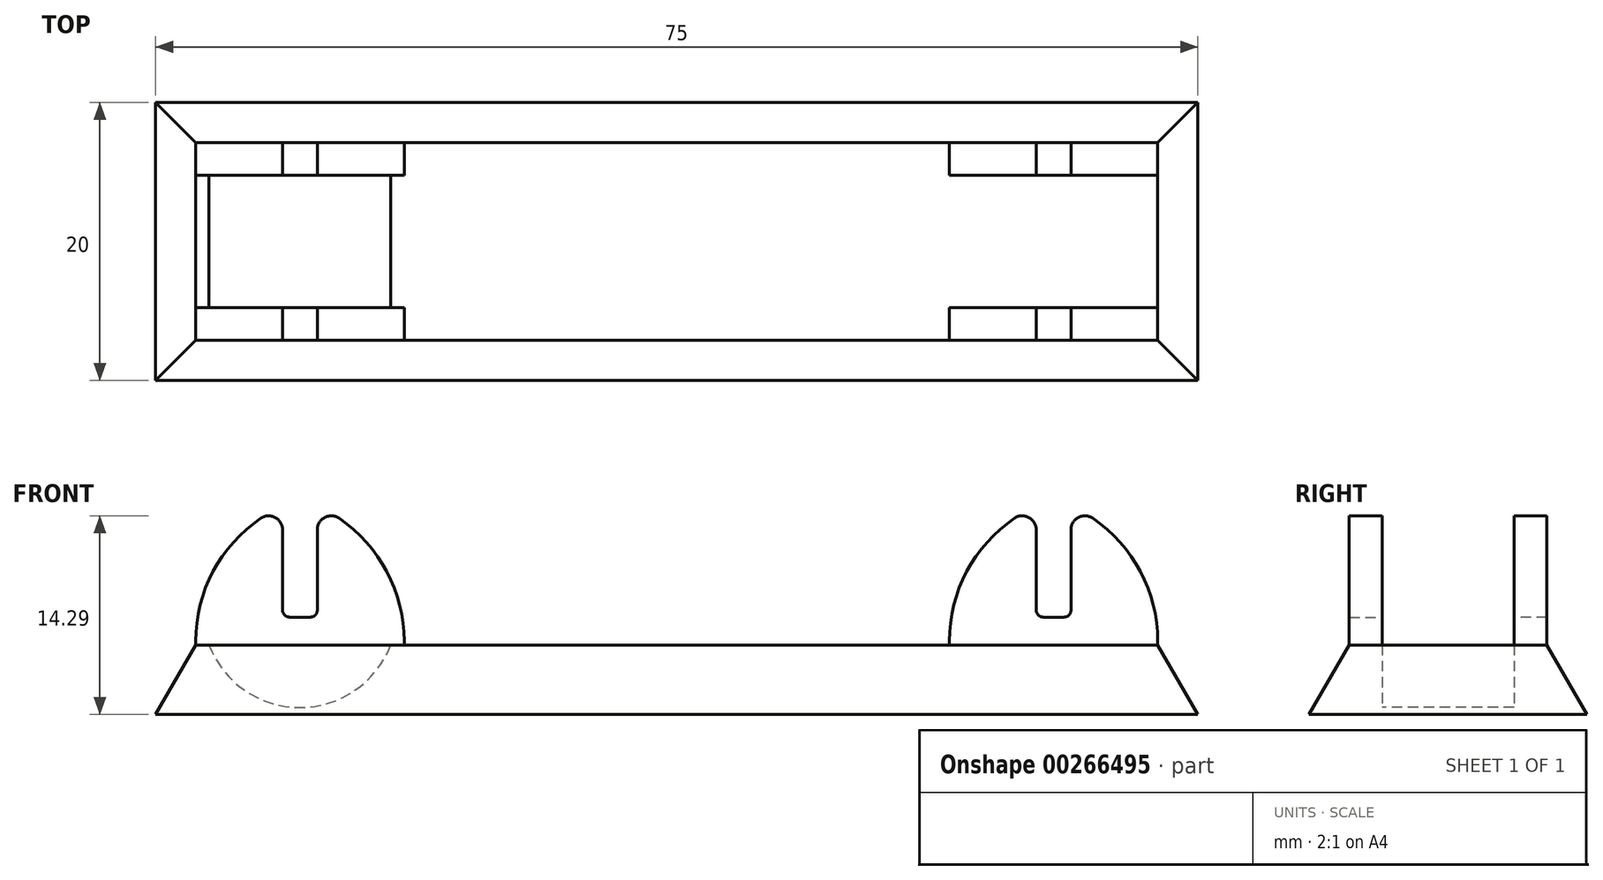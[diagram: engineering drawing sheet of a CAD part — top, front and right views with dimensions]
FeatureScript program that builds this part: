
annotation { "Feature Type Name" : "Feature", "Feature Type Description" : "" }
export const myFeature = defineFeature(function(context is Context, id is Id, definition is map)
    precondition{}
    {
        {
            var Q0;
            Q0=qCreatedBy(makeId("Top.planeOp"),FACE);
            var sketch = newSketch(context, id + "F0", { "sketchPlane" : qUnion([Q0])});
            skLineSegment(sketch, "E0.bottom", {"start": v(-37.5, 10) * mm, "end": v(37.5, 10) * mm});
            skLineSegment(sketch, "E0.top", {"start": v(-37.5, -10) * mm, "end": v(37.5, -10) * mm});
            skLineSegment(sketch, "E0.left", {"start": v(-37.5, 10) * mm, "end": v(-37.5, -10) * mm});
            skLineSegment(sketch, "E0.right", {"start": v(37.5, 10) * mm, "end": v(37.5, -10) * mm});
            skPoint(sketch, "E1", {"position": v(0, 10) * mm});
            skPoint(sketch, "E2", {"position": v(-37.5, 0) * mm});
            skSolve(sketch);
        }
        {
            var Q0;
            Q0=makeQuery(id+"F0.imprint","IMPRINT",FACE,{"disambiguationData":[TD([[makeQuery(id+"F0.imprint","IMPRINT",EDGE,{"derivedFrom":sQuery(id+"F0.wireOp",EDGE,"E0.bottom")}),-1.0]])]});
            extrude(context, id + "F1", {"entities" : qUnion([Q0]), "depth" : 5 * mm, "hasDraft" : true, "draftAngle" : 30 * degree, "draftPullDirection" : true});
        }
        {
            var Q0;
            Q0=makeQuery(id+"F1.opExtrude","CAP_FACE",FACE,{"disambiguationData":[OSD([sQuery(id+"F0.wireOp",EDGE,"E0.bottom"),sQuery(id+"F0.wireOp",EDGE,"E0.top"),sQuery(id+"F0.wireOp",EDGE,"E0.left"),sQuery(id+"F0.wireOp",EDGE,"E0.right")])],"isStart":false});
            var sketch = newSketch(context, id + "F2", { "sketchPlane" : qUnion([Q0])});
            skLineSegment(sketch, "E3.bottom", {"start": v(-34.61, 7.11) * mm, "end": v(-19.61, 7.11) * mm});
            skLineSegment(sketch, "E3.top", {"start": v(-34.61, 4.75) * mm, "end": v(-19.61, 4.75) * mm});
            skLineSegment(sketch, "E3.left", {"start": v(-34.61, 7.11) * mm, "end": v(-34.61, 4.75) * mm});
            skLineSegment(sketch, "E3.right", {"start": v(-19.61, 7.11) * mm, "end": v(-19.61, 4.75) * mm});
            skLineSegment(sketch, "E4", {"start": v(-57.2, 0) * mm, "end": v(85.15, 0) * mm, "construction": true});
            skLineSegment(sketch, "E5.MirrorCS", {"start": v(-19.61, -7.11) * mm, "end": v(-19.61, -4.75) * mm});
            skLineSegment(sketch, "E6.MirrorCS", {"start": v(-34.61, -7.11) * mm, "end": v(-19.61, -7.11) * mm});
            skLineSegment(sketch, "E7.MirrorCS", {"start": v(-34.61, -4.75) * mm, "end": v(-19.61, -4.75) * mm});
            skLineSegment(sketch, "E8.MirrorCS", {"start": v(-34.61, -7.11) * mm, "end": v(-34.61, -4.75) * mm});
            skSolve(sketch);
        }
        {
            var Q0;
            Q0=makeQuery(id+"F2.imprint","IMPRINT",FACE,{"disambiguationData":[TD([[makeQuery(id+"F2.imprint","IMPRINT",EDGE,{"derivedFrom":sQuery(id+"F2.wireOp",EDGE,"E3.bottom")}),-1.0]])]});
            var Q1;
            Q1=makeQuery(id+"F2.imprint","IMPRINT",FACE,{"disambiguationData":[TD([[makeQuery(id+"F2.imprint","IMPRINT",EDGE,{"derivedFrom":sQuery(id+"F2.wireOp",EDGE,"E5.MirrorCS")}),1.0]])]});
            extrude(context, id + "F3", {"entities" : qUnion([Q0, Q1]), "depth" : 10 * mm});
        }
        {
            var Q0;
            Q0=makeQuery(id+"F3.opExtrude","CAP_FACE",FACE,{"disambiguationData":[OSD([sQuery(id+"F2.wireOp",EDGE,"E3.bottom"),sQuery(id+"F2.wireOp",EDGE,"E3.top"),sQuery(id+"F2.wireOp",EDGE,"E3.left"),sQuery(id+"F2.wireOp",EDGE,"E3.right")])],"isStart":false});
            var sketch = newSketch(context, id + "F4", { "sketchPlane" : qUnion([Q0])});
            skLineSegment(sketch, "E9.bottom", {"start": v(-28.36, 7.11) * mm, "end": v(-25.86, 7.11) * mm});
            skLineSegment(sketch, "E9.top", {"start": v(-28.36, 4.75) * mm, "end": v(-25.86, 4.75) * mm});
            skLineSegment(sketch, "E9.left", {"start": v(-28.36, 7.11) * mm, "end": v(-28.36, 4.75) * mm});
            skLineSegment(sketch, "E9.right", {"start": v(-25.86, 7.11) * mm, "end": v(-25.86, 4.75) * mm});
            skPoint(sketch, "E10", {"position": v(-27.11, 7.11) * mm});
            skLineSegment(sketch, "E11", {"start": v(-40.4, 0) * mm, "end": v(-13.05, 0) * mm, "construction": true});
            skLineSegment(sketch, "E12.MirrorCS", {"start": v(-28.36, -7.11) * mm, "end": v(-25.86, -7.11) * mm});
            skPoint(sketch, "E13.MirrorP", {"position": v(-27.11, -7.11) * mm});
            skLineSegment(sketch, "E14.MirrorCS", {"start": v(-28.36, -7.11) * mm, "end": v(-28.36, -4.75) * mm});
            skLineSegment(sketch, "E15.MirrorCS", {"start": v(-25.86, -7.11) * mm, "end": v(-25.86, -4.75) * mm});
            skLineSegment(sketch, "E16.MirrorCS", {"start": v(-28.36, -4.75) * mm, "end": v(-25.86, -4.75) * mm});
            skSolve(sketch);
        }
        {
            var Q0;
            Q0 = qSketchRegion(id + "F4", true);
            extrude(context, id + "F5", {"entities" : qUnion([Q0]), "operationType" : NewBodyOperationType.REMOVE, "oppositeDirection" : true, "depth" : 8 * mm});
        }
        {
            var Q0;
            Q0=makeQuery(id+"F5.boolean.opBoolean","COPY",EDGE,{"derivedFrom":makeQuery(id+"F5.opExtrude","CAP_EDGE",EDGE,{"disambiguationData":[OSD([sQuery(id+"F4.wireOp",EDGE,"E9.left")])],"isStart":false})});
            var Q1;
            Q1=makeQuery(id+"F5.boolean.opBoolean","COPY",EDGE,{"derivedFrom":makeQuery(id+"F5.opExtrude","CAP_EDGE",EDGE,{"disambiguationData":[OSD([sQuery(id+"F4.wireOp",EDGE,"E14.MirrorCS")])],"isStart":false})});
            var Q2;
            Q2=makeQuery(id+"F5.boolean.opBoolean","COPY",EDGE,{"derivedFrom":makeQuery(id+"F5.opExtrude","CAP_EDGE",EDGE,{"disambiguationData":[OSD([sQuery(id+"F4.wireOp",EDGE,"E9.right")])],"isStart":false})});
            var Q3;
            Q3=makeQuery(id+"F5.boolean.opBoolean","COPY",EDGE,{"derivedFrom":makeQuery(id+"F5.opExtrude","CAP_EDGE",EDGE,{"disambiguationData":[OSD([sQuery(id+"F4.wireOp",EDGE,"E15.MirrorCS")])],"isStart":false})});
            fillet(context, id + "F6", {"entities" : qUnion([Q0, Q1, Q2, Q3]), "radius" : .5 * mm, "tangentPropagation" : true, "allowEdgeOverflow" : false});
        }
        {
            var Q0;
            Q0=makeQuery(id+"F3.opExtrude","CAP_EDGE",EDGE,{"disambiguationData":[OSD([sQuery(id+"F2.wireOp",EDGE,"E3.left")])],"isStart":false});
            var Q1;
            Q1=makeQuery(id+"F3.opExtrude","CAP_EDGE",EDGE,{"disambiguationData":[OSD([sQuery(id+"F2.wireOp",EDGE,"E8.MirrorCS")])],"isStart":false});
            var Q2;
            Q2=makeQuery(id+"F3.opExtrude","CAP_EDGE",EDGE,{"disambiguationData":[OSD([sQuery(id+"F2.wireOp",EDGE,"E5.MirrorCS")])],"isStart":false});
            var Q3;
            Q3=makeQuery(id+"F3.opExtrude","CAP_EDGE",EDGE,{"disambiguationData":[OSD([sQuery(id+"F2.wireOp",EDGE,"E3.right")])],"isStart":false});
            fillet(context, id + "F7", {"entities" : qUnion([Q0, Q1, Q2, Q3]), "radius" : 10.7 * mm, "tangentPropagation" : true, "allowEdgeOverflow" : false});
        }
        {
            var Q0;
            Q0=makeQuery(id+"F7.opFillet","BLEND_EDGE",EDGE,{"blendedFrom":[makeQuery(id+"F3.opExtrude","CAP_EDGE",EDGE,{"disambiguationData":[OSD([sQuery(id+"F2.wireOp",EDGE,"E3.left")])],"isStart":false}),makeQuery(id+"F5.boolean.opBoolean","COPY",FACE,{"derivedFrom":makeQuery(id+"F5.opExtrude","SWEPT_FACE",FACE,{"disambiguationData":[OSD([sQuery(id+"F4.wireOp",EDGE,"E9.left")])]})})],"blendedInto":[makeQuery(id+"F5.boolean.opBoolean","COPY",FACE,{"derivedFrom":makeQuery(id+"F5.opExtrude","SWEPT_FACE",FACE,{"disambiguationData":[OSD([sQuery(id+"F4.wireOp",EDGE,"E9.left")])]})})]});
            var Q1;
            Q1=makeQuery(id+"F7.opFillet","BLEND_EDGE",EDGE,{"blendedFrom":[makeQuery(id+"F3.opExtrude","CAP_EDGE",EDGE,{"disambiguationData":[OSD([sQuery(id+"F2.wireOp",EDGE,"E3.right")])],"isStart":false}),makeQuery(id+"F5.boolean.opBoolean","COPY",FACE,{"derivedFrom":makeQuery(id+"F5.opExtrude","SWEPT_FACE",FACE,{"disambiguationData":[OSD([sQuery(id+"F4.wireOp",EDGE,"E9.right")])]})})],"blendedInto":[makeQuery(id+"F5.boolean.opBoolean","COPY",FACE,{"derivedFrom":makeQuery(id+"F5.opExtrude","SWEPT_FACE",FACE,{"disambiguationData":[OSD([sQuery(id+"F4.wireOp",EDGE,"E9.right")])]})})]});
            var Q2;
            Q2=makeQuery(id+"F7.opFillet","BLEND_EDGE",EDGE,{"blendedFrom":[makeQuery(id+"F3.opExtrude","CAP_EDGE",EDGE,{"disambiguationData":[OSD([sQuery(id+"F2.wireOp",EDGE,"E8.MirrorCS")])],"isStart":false}),makeQuery(id+"F5.boolean.opBoolean","COPY",FACE,{"derivedFrom":makeQuery(id+"F5.opExtrude","SWEPT_FACE",FACE,{"disambiguationData":[OSD([sQuery(id+"F4.wireOp",EDGE,"E14.MirrorCS")])]})})],"blendedInto":[makeQuery(id+"F5.boolean.opBoolean","COPY",FACE,{"derivedFrom":makeQuery(id+"F5.opExtrude","SWEPT_FACE",FACE,{"disambiguationData":[OSD([sQuery(id+"F4.wireOp",EDGE,"E14.MirrorCS")])]})})]});
            var Q3;
            Q3=makeQuery(id+"F7.opFillet","BLEND_EDGE",EDGE,{"blendedFrom":[makeQuery(id+"F3.opExtrude","CAP_EDGE",EDGE,{"disambiguationData":[OSD([sQuery(id+"F2.wireOp",EDGE,"E5.MirrorCS")])],"isStart":false}),makeQuery(id+"F5.boolean.opBoolean","COPY",FACE,{"derivedFrom":makeQuery(id+"F5.opExtrude","SWEPT_FACE",FACE,{"disambiguationData":[OSD([sQuery(id+"F4.wireOp",EDGE,"E15.MirrorCS")])]})})],"blendedInto":[makeQuery(id+"F5.boolean.opBoolean","COPY",FACE,{"derivedFrom":makeQuery(id+"F5.opExtrude","SWEPT_FACE",FACE,{"disambiguationData":[OSD([sQuery(id+"F4.wireOp",EDGE,"E15.MirrorCS")])]})})]});
            fillet(context, id + "F8", {"entities" : qUnion([Q0, Q1, Q2, Q3]), "radius" : 1 * mm, "tangentPropagation" : true, "allowEdgeOverflow" : false});
        }
        {
            var Q0;
            Q0=makeQuery(id+"F5.boolean.opBoolean","COPY",FACE,{"derivedFrom":makeQuery(id+"F5.opExtrude","CAP_FACE",FACE,{"disambiguationData":[OSD([sQuery(id+"F4.wireOp",EDGE,"E9.bottom"),sQuery(id+"F4.wireOp",EDGE,"E9.top"),sQuery(id+"F4.wireOp",EDGE,"E9.left"),sQuery(id+"F4.wireOp",EDGE,"E9.right")])],"isStart":false})});
            cPlane(context, id + "F9", {"entities" : qUnion([Q0]), "cplaneType" : CPlaneType.OFFSET, "offset" : .5 * mm, "width" : 150 * mm, "height" : 150 * mm});
        }
        {
            var Q0;
            Q0=qCreatedBy(id+"F9.planeOp",FACE);
            var sketch = newSketch(context, id + "F10", { "sketchPlane" : qUnion([Q0])});
            skLineSegment(sketch, "E17", {"start": v(-27.11, 16.1) * mm, "end": v(-27.11, -9.88) * mm, "construction": true});
            skLineSegment(sketch, "E18.bottom", {"start": v(-27.11, 4.75) * mm, "end": v(-20.11, 4.75) * mm});
            skLineSegment(sketch, "E18.top", {"start": v(-27.11, -4.75) * mm, "end": v(-20.11, -4.75) * mm});
            skLineSegment(sketch, "E18.left", {"start": v(-27.11, 4.75) * mm, "end": v(-27.11, -4.75) * mm});
            skLineSegment(sketch, "E18.right", {"start": v(-20.11, 4.75) * mm, "end": v(-20.11, -4.75) * mm});
            skPoint(sketch, "E19", {"position": v(-20.11, 0) * mm});
            skSolve(sketch);
        }
        {
            var Q0;
            Q0 = qSketchRegion(id + "F10", true);
            var Q1;
            Q1=sQuery(id+"F10.wireOp",EDGE,"E17");
            revolve(context, id + "F11", {"operationType" : NewBodyOperationType.REMOVE, "entities" : qUnion([Q0]), "axis" : qUnion([Q1]), "revolveType" : RevolveType.FULL, "oppositeDirection" : true});
        }
        {
            var Q0;
            Q0=makeQuery(id+"F3.opExtrude","SWEPT_BODY",BODY,{"disambiguationData":[OSD([sQuery(id+"F2.wireOp",EDGE,"E3.bottom"),sQuery(id+"F2.wireOp",EDGE,"E3.top"),sQuery(id+"F2.wireOp",EDGE,"E3.left"),sQuery(id+"F2.wireOp",EDGE,"E3.right")])]});
            var Q1;
            Q1=makeQuery(id+"F3.opExtrude","SWEPT_BODY",BODY,{"disambiguationData":[OSD([sQuery(id+"F2.wireOp",EDGE,"E5.MirrorCS"),sQuery(id+"F2.wireOp",EDGE,"E6.MirrorCS"),sQuery(id+"F2.wireOp",EDGE,"E7.MirrorCS"),sQuery(id+"F2.wireOp",EDGE,"E8.MirrorCS")])]});
            var Q2;
            Q2=qCreatedBy(makeId("Right.planeOp"),FACE);
            mirror(context, id + "F12", {"operationType" : NewBodyOperationType.ADD, "entities" : qUnion([Q0, Q1]), "mirrorPlane" : qUnion([Q2])});
        }
    });
